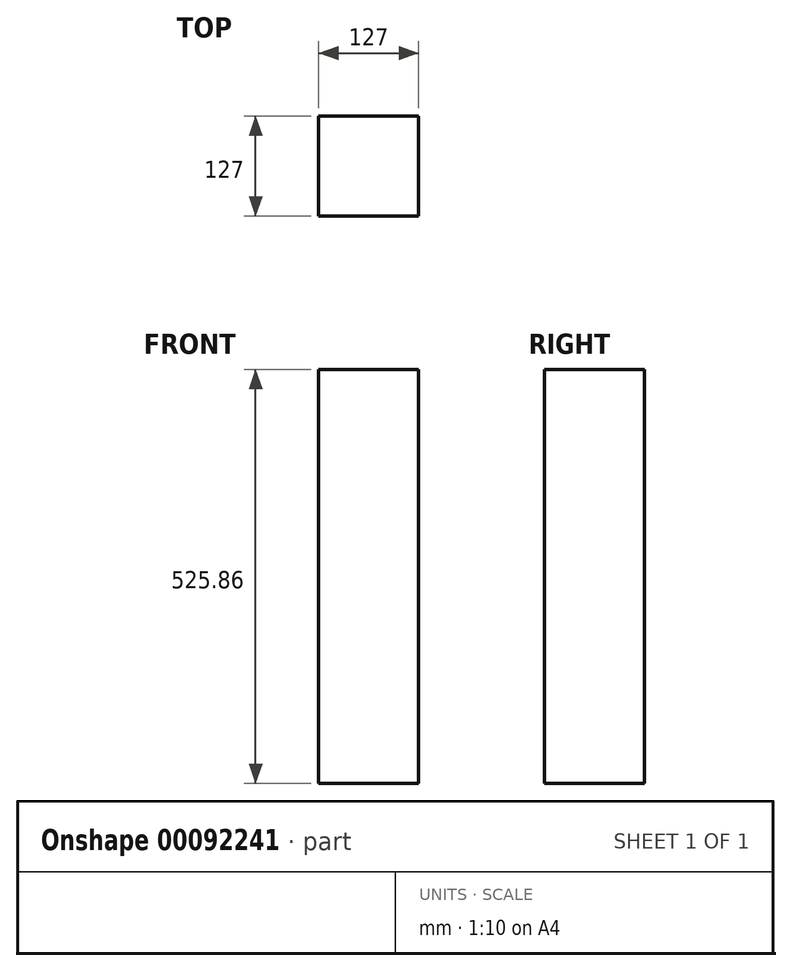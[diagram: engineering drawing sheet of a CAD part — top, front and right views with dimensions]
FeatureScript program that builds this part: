
annotation { "Feature Type Name" : "Feature", "Feature Type Description" : "" }
export const myFeature = defineFeature(function(context is Context, id is Id, definition is map)
    precondition{}
    {
        {
            var Q0;
            Q0=qCreatedBy(makeId("Front.planeOp"),FACE);
            var sketch = newSketch(context, id + "F0", { "sketchPlane" : qUnion([Q0])});
            skLineSegment(sketch, "E0.bottom", {"start": v(-46.61, 444.92) * mm, "end": v(80.39, 444.92) * mm});
            skLineSegment(sketch, "E0.top", {"start": v(-46.61, -80.94) * mm, "end": v(80.39, -80.94) * mm});
            skLineSegment(sketch, "E0.left", {"start": v(-46.61, 444.92) * mm, "end": v(-46.61, -80.94) * mm});
            skLineSegment(sketch, "E0.right", {"start": v(80.39, 444.92) * mm, "end": v(80.39, -80.94) * mm});
            skSolve(sketch);
        }
        {
            var Q0;
            Q0 = qSketchRegion(id + "F0", true);
            extrude(context, id + "F1", {"entities" : qUnion([Q0]), "depth" : 127 * mm});
        }
    });
